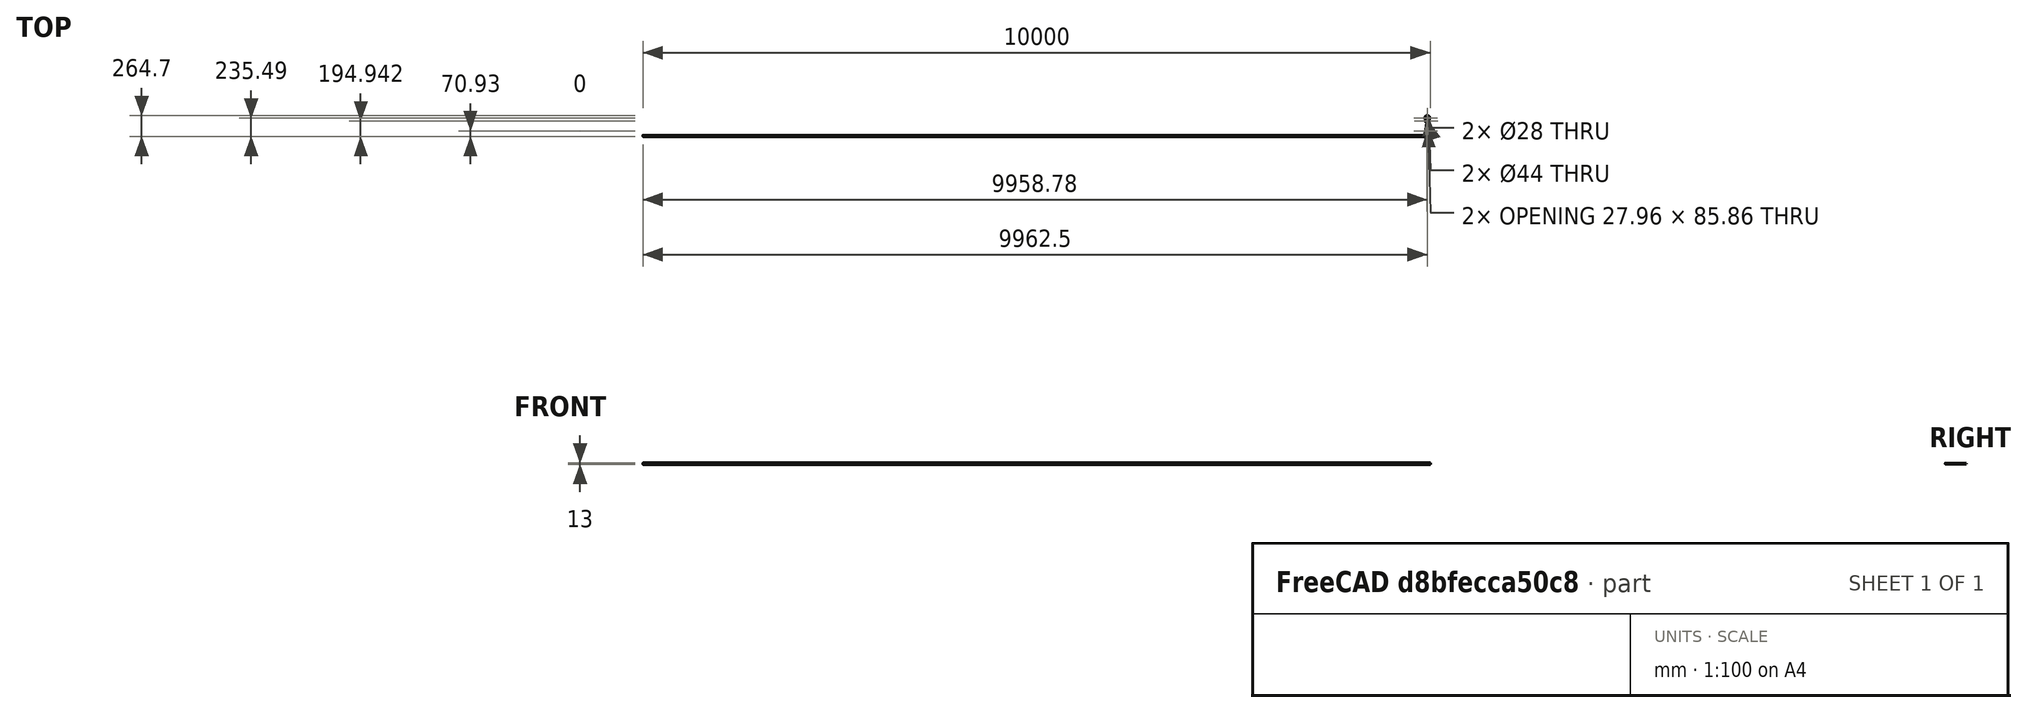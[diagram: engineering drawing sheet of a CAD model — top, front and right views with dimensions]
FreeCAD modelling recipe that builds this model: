
FCSTD DOCUMENT  (FreeCAD 0.16R)
Label: WheelTemplate406-60
License: All rights reserved
LicenseURL: http://en.wikipedia.org/wiki/All_rights_reserved
objects: Sketcher::SketchObject×4, PartDesign::Fillet×4, PartDesign::Pocket×3, PartDesign::Chamfer×2, PartDesign::Pad×1, Mesh::Feature×1
note: 18 computed .brp shape members not serialized (recipe doc carries the construction recipe); baked Part::Feature solids carry a one-line shape summary decoded from their .brp

FEATURE [Sketcher::SketchObject] Sketch
  sketch-geometry (15):
    g0: LineSegment StartX=-25 StartY=34 StartZ=0 EndX=-3.33777 EndY=161.98 EndZ=0
    g1: LineSegment StartX=19 StartY=28 StartZ=0 EndX=2.45367 EndY=161.851 EndZ=0
    g2: LineSegment [constr] StartX=-25 StartY=251.7 StartZ=0 EndX=25 EndY=251.7 EndZ=0
    g3: LineSegment StartX=-37.5 StartY=-5 StartZ=0 EndX=37.5 EndY=-5 EndZ=0
    g4: LineSegment StartX=19 StartY=28 StartZ=0 EndX=19 EndY=8 EndZ=0
    g5: LineSegment StartX=-25 StartY=34 StartZ=0 EndX=-25 EndY=8 EndZ=0
    g6: LineSegment StartX=37.5 StartY=-5 StartZ=0 EndX=37.5 EndY=8 EndZ=0
    g7: LineSegment StartX=37.5 StartY=8 StartZ=0 EndX=19 EndY=8 EndZ=0
    g8: LineSegment StartX=-37.5 StartY=-5 StartZ=0 EndX=-37.5 EndY=8 EndZ=0
    g9: LineSegment StartX=-37.5 StartY=8 StartZ=0 EndX=-25 EndY=8 EndZ=0
    g10: LineSegment [constr] StartX=-3.33777 StartY=161.98 StartZ=0 EndX=0 EndY=181.7 EndZ=0
    g11: LineSegment [constr] StartX=2.45367 StartY=161.851 StartZ=0 EndX=0 EndY=181.7 EndZ=0
    g12: ArcOfCircle CenterX=0 CenterY=221.7 CenterZ=0 NormalX=0 NormalY=0 NormalZ=1 Radius=30 StartAngle=5.21775 EndAngle=10.4902
    g13: ArcOfCircle CenterX=0 CenterY=181.7 CenterZ=0 NormalX=0 NormalY=0 NormalZ=1 Radius=20 StartAngle=4.83538 EndAngle=7.04123
    g14: ArcOfCircle CenterX=0 CenterY=181.7 CenterZ=0 NormalX=0 NormalY=0 NormalZ=1 Radius=20 StartAngle=2.38355 EndAngle=4.54472
  constraints (50):
    c: Horizontal(g2)
    c: Symmetric(g2,g2,g-2)
    c: DistanceY(g-1,g2) = 251.7
    c: Distance(g2) = 50
    c: Horizontal(g3)
    c: Coincident(g4,g1)
    c: Coincident(g5,g0)
    c: Vertical(g5)
    c: Vertical(g4)
    c: DistanceX(g4) = 19
    c: DistanceX(g5) = -25
    c: Distance(g3) = 75
    c: Vertical(g6)
    c: Coincident(g6,g7)
    c: PointOnObject(g7,g4)
    c: Horizontal(g7)
    c: Coincident(g8,g9)
    c: PointOnObject(g9,g5)
    c: Horizontal(g9)
    c: Vertical(g8)
    c: DistanceY(g8) = 8
    c: DistanceY(g6) = 8
    c: Coincident(g4,g7)
    c: Coincident(g5,g9)
    c: Distance(g5) = 26
    c: Distance(g4) = 20
    c: Coincident(g8,g3)
    c: Coincident(g6,g3)
    c: Symmetric(g3,g3,g-2)
    c: DistanceY(g3) = -5
    c: PointOnObject(g11,g-2)
    c: Coincident(g1,g11)
    c: Parallel(g11,g1)
    c: Parallel(g0,g10)
    c: Coincident(g11,g10)
    c: Distance(g10,g2) = 70
    c: PointOnObject(g12,g-2)
    c: Radius(g12) = 30
    c: Tangent(g12,g2)
    c: PointOnObject(g13,g-2)
    c: Coincident(g13,g10)
    c: Radius(g13) = 20
    c: Equal(g13,g14)
    c: Coincident(g13,g12)
    c: Coincident(g14,g12)
    c: Coincident(g13,g14)
    c: Symmetric(g12,g12,g-2)
    c: Coincident(g0,g10)
    c: Coincident(g0,g14)
    c: Coincident(g1,g13)
FEATURE [PartDesign::Pad] Pad
  Length = 10
  Length2 = 100
  Sketch = -> Sketch
  Type = 0
FEATURE [Sketcher::SketchObject] Sketch001
  ExternalGeometry = -> [Pad]
  Placement = pos=(37.5,0,0) rot=(0.57735,0.57735,0.57735;2.0944rad)
  Support = -> Pad [Face11]
  sketch-geometry (1):
    g0: Circle CenterX=-6.5 CenterY=5 CenterZ=0 NormalX=0 NormalY=0 NormalZ=1 Radius=6.5
  constraints (3):
    c: Radius(g0) = 6.5
    c: DistanceY(g0) = 5
    c: Tangent(g-2,g0)
FEATURE [PartDesign::Pocket] Pocket
  Length = 5
  Sketch = -> Sketch001
  Type = 1
FEATURE [Sketcher::SketchObject] Sketch002
  ExternalGeometry = -> [Pocket]
  Placement = pos=(0,0,10) rot=(0,0,1;0rad)
  Support = -> Pocket [Face4]
  sketch-geometry (5):
    g0: Circle CenterX=0 CenterY=222.49 CenterZ=0 NormalX=0 NormalY=0 NormalZ=1 Radius=22
    g1: Circle CenterX=0 CenterY=181.942 CenterZ=0 NormalX=0 NormalY=0 NormalZ=1 Radius=14
    g2: LineSegment StartX=-1.54243 StartY=112.667 StartZ=0 EndX=-18.0737 EndY=15 EndZ=0
    g3: LineSegment StartX=-18.0737 StartY=15 StartZ=0 EndX=10.5309 EndY=15 EndZ=0
    g4: LineSegment StartX=10.5309 StartY=15 StartZ=0 EndX=-1.54243 EndY=112.667 EndZ=0
  constraints (13):
    c: Coincident(g2,g3)
    c: Horizontal(g3)
    c: Coincident(g3,g4)
    c: Coincident(g4,g2)
    c: Radius(g0) = 22
    c: PointOnObject(g1,g-2)
    c: PointOnObject(g0,g-2)
    c: Parallel(g4,g-3)
    c: Parallel(g2,g-4)
    c: DistanceY(g3) = 15
    c: Radius(g1) = 14
    c: Distance(g-4,g2) = 10
    c: Distance(g-3,g4) = 10
FEATURE [PartDesign::Pocket] Pocket001
  Length = 5
  Sketch = -> Sketch002
  Type = 1
FEATURE [PartDesign::Fillet] Fillet
  Base = -> Pocket001 [Edge53,Edge54,Edge52]
  Radius = 2
FEATURE [PartDesign::Fillet] Fillet001
  Base = -> Fillet [Edge42,Edge44]
  Radius = 2
FEATURE [PartDesign::Fillet] Fillet002
  Base = -> Fillet001 [Edge57,Edge22,Edge44,Edge53]
  Radius = 2
FEATURE [Sketcher::SketchObject] Sketch003
  Placement = pos=(0,0,10) rot=(0,0,1;0rad)
  Support = -> Fillet002 [Face26]
  sketch-geometry (3):
    g0: LineSegment StartX=0 StartY=3 StartZ=0 EndX=5 EndY=-15 EndZ=0
    g1: LineSegment StartX=5 StartY=-15 StartZ=0 EndX=-5 EndY=-15 EndZ=0
    g2: LineSegment StartX=-5 StartY=-15 StartZ=0 EndX=0 EndY=3 EndZ=0
  constraints (9):
    c: Coincident(g0,g1)
    c: Horizontal(g1)
    c: Coincident(g1,g2)
    c: Coincident(g2,g0)
    c: Symmetric(g1,g0,g-2)
    c: PointOnObject(g0,g-2)
    c: Distance(g1) = 10
    c: DistanceY(g0) = -15
    c: DistanceY(g0) = 3
FEATURE [PartDesign::Pocket] Pocket002
  Length = 5
  Sketch = -> Sketch003
  Type = 1
FEATURE [PartDesign::Fillet] Fillet003
  Base = -> Pocket002 [Edge57]
  Radius = 0.5
FEATURE [PartDesign::Chamfer] Chamfer
  Base = -> Fillet003 [Edge90,Edge89,Edge3,Edge6]
  Size = 1
FEATURE [PartDesign::Chamfer] Chamfer001
  Base = -> Chamfer [Edge46,Edge47,Edge33,Edge32]
  Size = 0.2
FEATURE [Mesh::Feature] Mesh  label="Chamfer001 (Meshed)"
